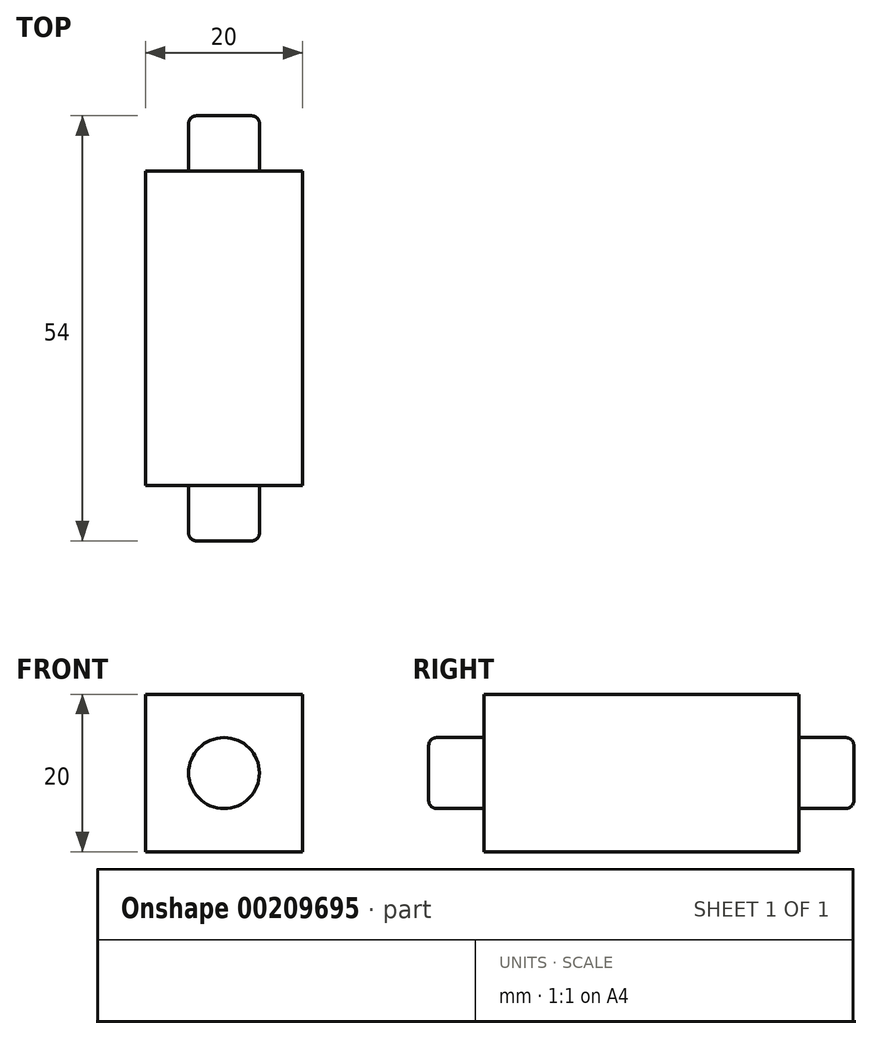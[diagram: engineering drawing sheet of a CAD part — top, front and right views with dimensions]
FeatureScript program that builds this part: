
annotation { "Feature Type Name" : "Feature", "Feature Type Description" : "" }
export const myFeature = defineFeature(function(context is Context, id is Id, definition is map)
    precondition{}
    {
        {
            var Q0;
            Q0=qCreatedBy(makeId("Front.planeOp"),FACE);
            var sketch = newSketch(context, id + "F0", { "sketchPlane" : qUnion([Q0])});
            skLineSegment(sketch, "E0.bottom", {"start": v(-10, 10) * mm, "end": v(10, 10) * mm});
            skLineSegment(sketch, "E0.top", {"start": v(-10, -10) * mm, "end": v(10, -10) * mm});
            skLineSegment(sketch, "E0.left", {"start": v(-10, 10) * mm, "end": v(-10, -10) * mm});
            skLineSegment(sketch, "E0.right", {"start": v(10, 10) * mm, "end": v(10, -10) * mm});
            skPoint(sketch, "E0.middle", {"position": v(0, 0) * mm});
            skSolve(sketch);
        }
        {
            var Q0;
            Q0=makeQuery(id+"F0.imprint","IMPRINT",FACE,{"disambiguationData":[TD([[makeQuery(id+"F0.imprint","IMPRINT",EDGE,{"derivedFrom":sQuery(id+"F0.wireOp",EDGE,"E0.bottom")}),-1.0]])]});
            extrude(context, id + "F1", {"entities" : qUnion([Q0]), "depth" : 40 * mm});
        }
        {
            var Q0;
            Q0=makeQuery(id+"F1.opExtrude","CAP_FACE",FACE,{"disambiguationData":[OSD([sQuery(id+"F0.wireOp",EDGE,"E0.bottom"),sQuery(id+"F0.wireOp",EDGE,"E0.top"),sQuery(id+"F0.wireOp",EDGE,"E0.left"),sQuery(id+"F0.wireOp",EDGE,"E0.right")])],"isStart":false});
            var sketch = newSketch(context, id + "F2", { "sketchPlane" : qUnion([Q0])});
            skCircle(sketch, "E1", {"center": v(0, 0) * mm, "radius": 4.5 * mm});
            skSolve(sketch);
        }
        {
            var Q0;
            Q0=makeQuery(id+"F2.imprint","IMPRINT",FACE,{"disambiguationData":[TD([[makeQuery(id+"F2.imprint","IMPRINT",EDGE,{"derivedFrom":sQuery(id+"F2.wireOp",EDGE,"E1")}),1.0]])]});
            extrude(context, id + "F3", {"entities" : qUnion([Q0]), "operationType" : NewBodyOperationType.ADD, "depth" : 7 * mm});
        }
        {
            var Q0;
            Q0=makeQuery(id+"F1.opExtrude","CAP_FACE",FACE,{"disambiguationData":[OSD([sQuery(id+"F0.wireOp",EDGE,"E0.bottom"),sQuery(id+"F0.wireOp",EDGE,"E0.top"),sQuery(id+"F0.wireOp",EDGE,"E0.left"),sQuery(id+"F0.wireOp",EDGE,"E0.right")])],"isStart":true});
            var sketch = newSketch(context, id + "F4", { "sketchPlane" : qUnion([Q0])});
            skCircle(sketch, "E2", {"center": v(0, 0) * mm, "radius": 4.5 * mm});
            skSolve(sketch);
        }
        {
            var Q0;
            Q0=makeQuery(id+"F4.imprint","IMPRINT",FACE,{"disambiguationData":[TD([[makeQuery(id+"F4.imprint","IMPRINT",EDGE,{"derivedFrom":sQuery(id+"F4.wireOp",EDGE,"E2")}),1.0]])]});
            extrude(context, id + "F5", {"entities" : qUnion([Q0]), "operationType" : NewBodyOperationType.ADD, "depth" : 7 * mm});
        }
        {
            var Q0;
            Q0=makeQuery(id+"F5.opExtrude","CAP_FACE",FACE,{"disambiguationData":[OSD([sQuery(id+"F4.wireOp",EDGE,"E2")])],"isStart":false});
            var Q1;
            Q1=makeQuery(id+"F3.opExtrude","CAP_EDGE",EDGE,{"disambiguationData":[OSD([sQuery(id+"F2.wireOp",EDGE,"E1")])],"isStart":false});
            fillet(context, id + "F6", {"entities" : qUnion([Q0, Q1]), "radius" : 1 * mm, "tangentPropagation" : true, "allowEdgeOverflow" : false});
        }
    });
